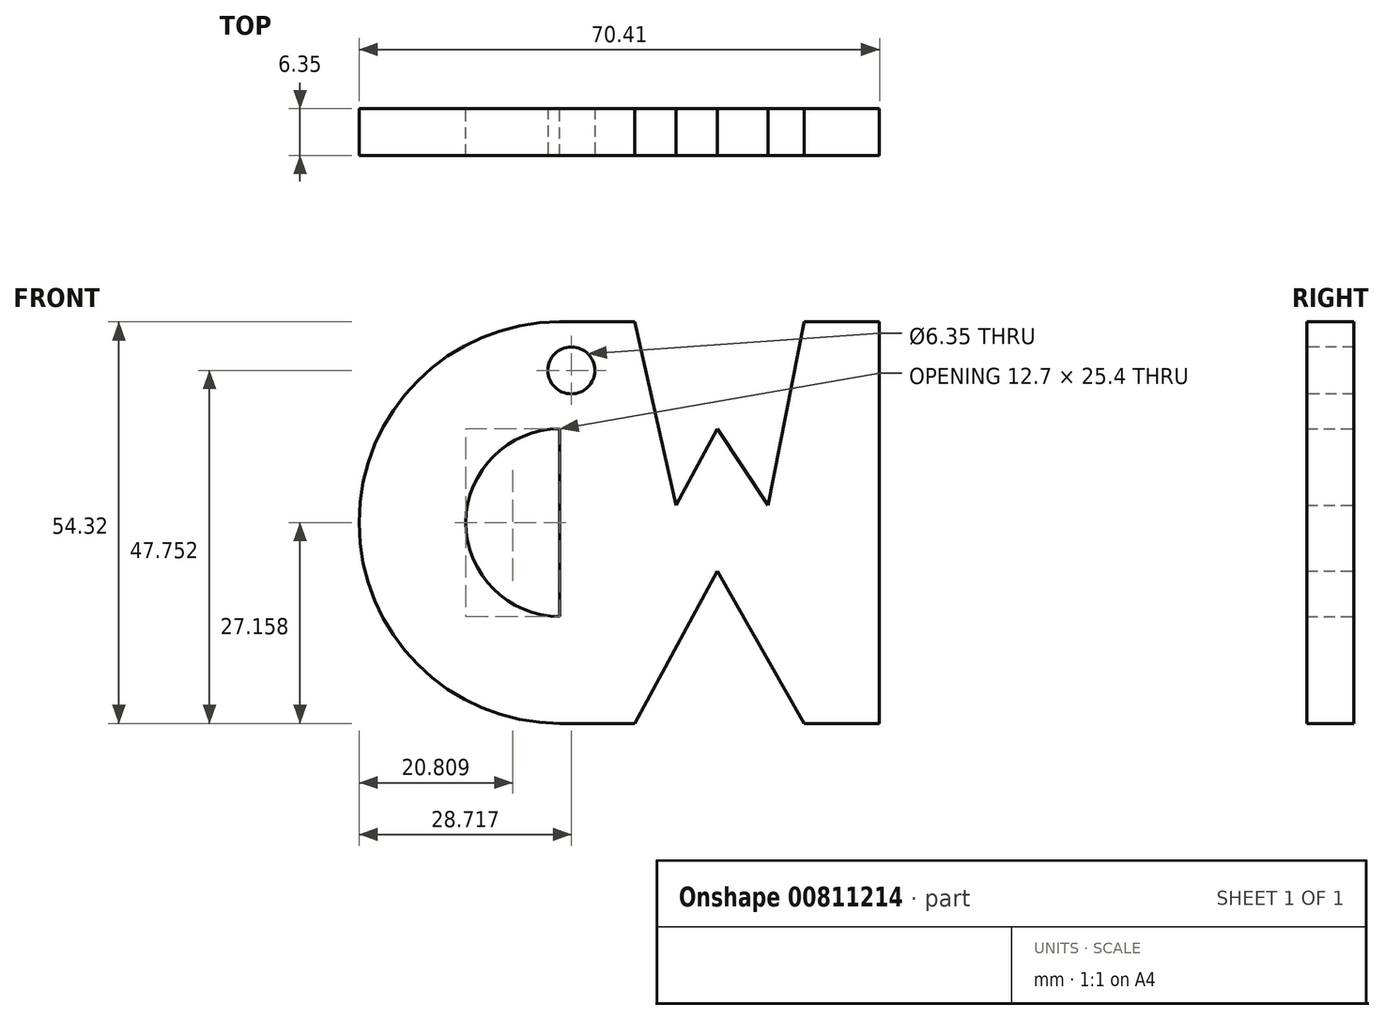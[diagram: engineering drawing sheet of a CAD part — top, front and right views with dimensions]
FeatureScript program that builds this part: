
annotation { "Feature Type Name" : "Feature", "Feature Type Description" : "" }
export const myFeature = defineFeature(function(context is Context, id is Id, definition is map)
    precondition{}
    {
        {
            var Q0;
            Q0=qCreatedBy(makeId("Front.planeOp"),FACE);
            var sketch = newSketch(context, id + "F0", { "sketchPlane" : qUnion([Q0])});
            skLineSegment(sketch, "E0", {"start": v(38.67, 52.93) * mm, "end": v(38.67, 45.3) * mm});
            skArc(sketch, "E1", {"start": v(38.67, 52.93) * mm, "mid": v(11.51, 25.77) * mm, "end": v(38.67, -1.39) * mm});
            skLineSegment(sketch, "E2", {"start": v(38.67, 6.23) * mm, "end": v(38.67, -1.39) * mm});
            skLineSegment(sketch, "E3", {"start": v(38.67, 45.3) * mm, "end": v(38.67, 6.23) * mm});
            skArc(sketch, "E4", {"start": v(38.67, 38.47) * mm, "mid": v(25.97, 25.77) * mm, "end": v(38.67, 13.07) * mm});
            skLineSegment(sketch, "E5", {"start": v(38.67, 52.93) * mm, "end": v(48.83, 52.93) * mm});
            skLineSegment(sketch, "E6", {"start": v(48.83, 52.93) * mm, "end": v(54.4, 28.15) * mm});
            skLineSegment(sketch, "E7", {"start": v(54.4, 28.15) * mm, "end": v(60, 38.47) * mm});
            skLineSegment(sketch, "E8", {"start": v(60, 38.47) * mm, "end": v(66.83, 28.15) * mm});
            skLineSegment(sketch, "E9", {"start": v(66.83, 28.15) * mm, "end": v(71.76, 52.93) * mm});
            skLineSegment(sketch, "E10", {"start": v(71.76, 52.93) * mm, "end": v(81.92, 52.93) * mm});
            skLineSegment(sketch, "E11", {"start": v(38.67, -1.39) * mm, "end": v(48.83, -1.39) * mm});
            skLineSegment(sketch, "E12", {"start": v(38.67, 52.93) * mm, "end": v(38.67, -1.39) * mm});
            skLineSegment(sketch, "E13", {"start": v(81.92, 52.93) * mm, "end": v(81.92, -1.39) * mm});
            skLineSegment(sketch, "E14", {"start": v(81.92, -1.39) * mm, "end": v(71.76, -1.39) * mm});
            skLineSegment(sketch, "E15", {"start": v(48.83, -1.39) * mm, "end": v(60, 19.22) * mm});
            skLineSegment(sketch, "E16", {"start": v(71.76, -1.39) * mm, "end": v(60, 19.22) * mm});
            skSolve(sketch);
        }
        {
            var Q0;
            {var subQ6=sQuery(id+"F0.wireOp",EDGE,"E5");Q0=makeQuery(id+"F0.imprint","IMPRINT",FACE,{"disambiguationData":[TD([[makeQuery(id+"F0.imprint","IMPRINT",EDGE,{"derivedFrom":subQ6}),-1.0]])]});}
            var Q1;
            {var subQ0=sQuery(id+"F0.wireOp",EDGE,"E1");Q1=makeQuery(id+"F0.imprint","IMPRINT",FACE,{"disambiguationData":[TD([[makeQuery(id+"F0.imprint","IMPRINT",EDGE,{"derivedFrom":subQ0}),1.0]])]});}
            extrude(context, id + "F1", {"entities" : qUnion([Q0, Q1]), "depth" : 6.35 * mm, "offsetDistance" : 25.4 * mm});
        }
        {
            var Q0;
            Q0=makeQuery(id+"F1.opExtrude","CAP_FACE",FACE,{"disambiguationData":[OSD([sQuery(id+"F0.wireOp",EDGE,"E1"),sQuery(id+"F0.wireOp",EDGE,"E4"),sQuery(id+"F0.wireOp",EDGE,"E5"),sQuery(id+"F0.wireOp",EDGE,"E6"),sQuery(id+"F0.wireOp",EDGE,"E7"),sQuery(id+"F0.wireOp",EDGE,"E8"),sQuery(id+"F0.wireOp",EDGE,"E9"),sQuery(id+"F0.wireOp",EDGE,"E10"),sQuery(id+"F0.wireOp",EDGE,"E11"),sQuery(id+"F0.wireOp",EDGE,"E12"),sQuery(id+"F0.wireOp",EDGE,"E13"),sQuery(id+"F0.wireOp",EDGE,"E14"),sQuery(id+"F0.wireOp",EDGE,"E15"),sQuery(id+"F0.wireOp",EDGE,"E16")])],"isStart":false});
            var sketch = newSketch(context, id + "F2", { "sketchPlane" : qUnion([Q0])});
            skCircle(sketch, "E17", {"center": v(40.23, 46.36) * mm, "radius": 3.18 * mm});
            skSolve(sketch);
        }
        {
            var Q0;
            Q0 = qSketchRegion(id + "F2", true);
            extrude(context, id + "F3", {"entities" : qUnion([Q0]), "operationType" : NewBodyOperationType.REMOVE, "endBound" : BoundingType.THROUGH_ALL, "oppositeDirection" : true, "depth" : 25.4 * mm, "offsetDistance" : 25.4 * mm});
        }
    });
